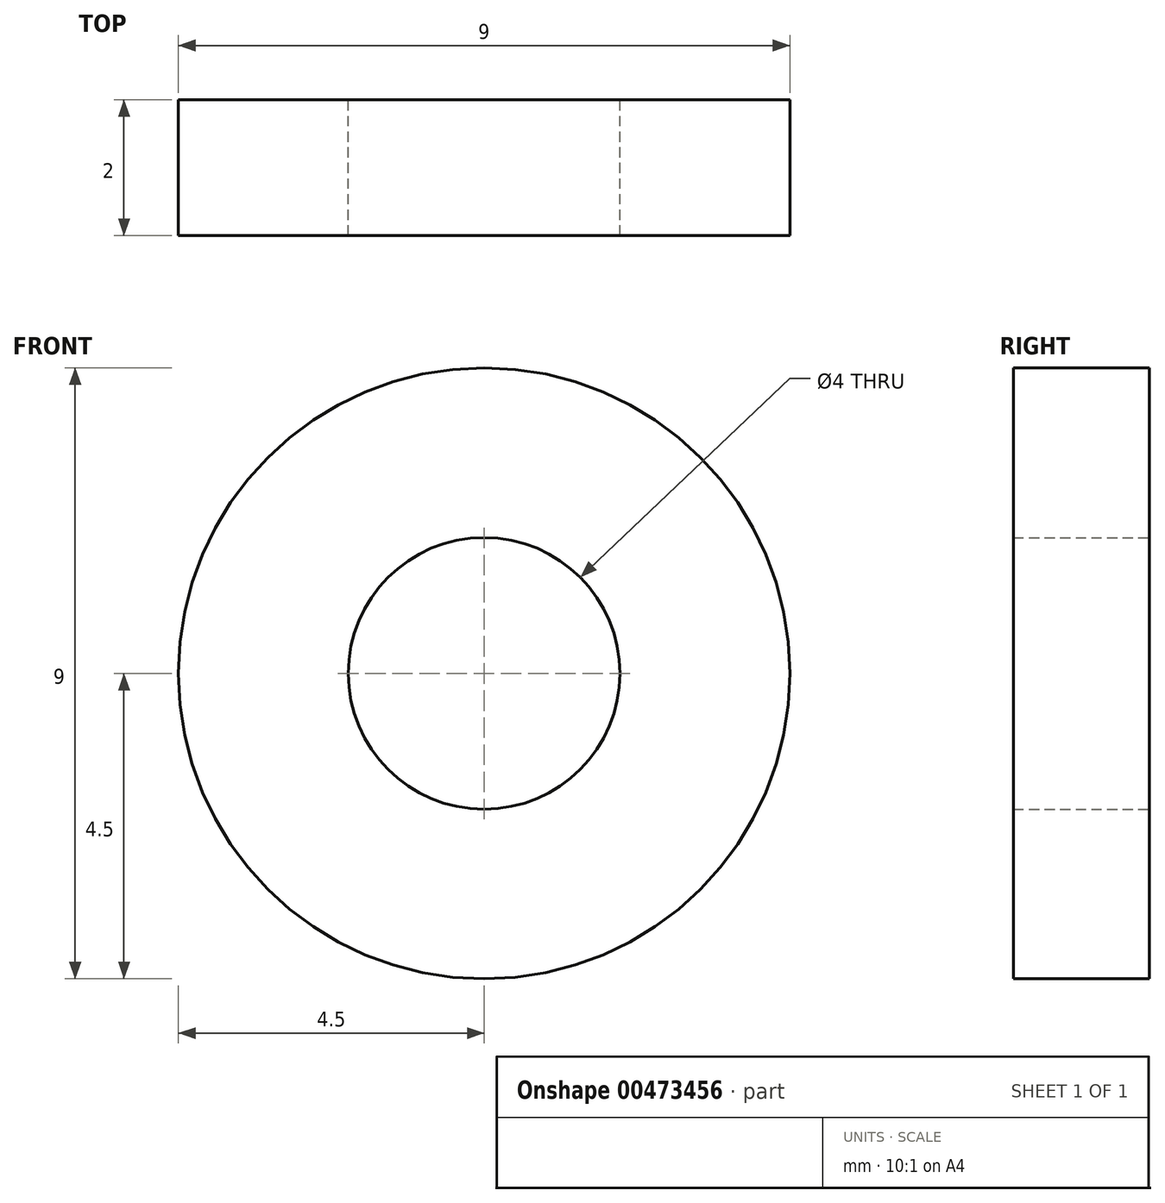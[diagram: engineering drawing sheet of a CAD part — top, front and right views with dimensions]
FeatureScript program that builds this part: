
annotation { "Feature Type Name" : "Feature", "Feature Type Description" : "" }
export const myFeature = defineFeature(function(context is Context, id is Id, definition is map)
    precondition{}
    {
        {
            var Q0;
            Q0=qCreatedBy(makeId("Front.planeOp"),FACE);
            var sketch = newSketch(context, id + "F0", { "sketchPlane" : qUnion([Q0])});
            skCircle(sketch, "E0", {"center": v(0, 0) * mm, "radius": 4.5 * mm});
            skSolve(sketch);
        }
        {
            var Q0;
            Q0 = qSketchRegion(id + "F0", true);
            extrude(context, id + "F1", {"entities" : qUnion([Q0]), "depth" : 2 * mm, "offsetDistance" : 25 * mm});
        }
        {
            var Q0;
            Q0=makeQuery(id+"F1.opExtrude","CAP_FACE",FACE,{"disambiguationData":[OSD([sQuery(id+"F0.wireOp",EDGE,"E0")])],"isStart":true});
            var sketch = newSketch(context, id + "F2", { "sketchPlane" : qUnion([Q0])});
            skCircle(sketch, "E1", {"center": v(0, 0) * mm, "radius": 2 * mm});
            skSolve(sketch);
        }
        {
            var Q0;
            Q0=sQuery(id+"F2.wireOp",VERTEX,"E1.center");
            var Q1;
            Q1=makeQuery(id+"F1.opExtrude","SWEPT_BODY",BODY,{"disambiguationData":[OSD([sQuery(id+"F0.wireOp",EDGE,"E0")])]});
            hole(context, id + "F3", {"style" : HoleStyle.SIMPLE, "endStyle" : HoleEndStyle.THROUGH, "holeDiameter" : 4 * mm, "majorDiameter" : 5 * mm, "isTappedThrough" : true, "tappedDepth" : 12 * mm, "tapClearance" : 3, "locations" : qUnion([Q0]), "scope" : qUnion([Q1])});
        }
    });
